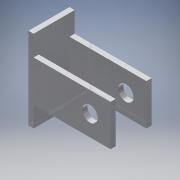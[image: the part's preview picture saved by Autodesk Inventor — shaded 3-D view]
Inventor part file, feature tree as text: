
AUTODESK INVENTOR PART (.ipt)
format: ipt  version: 2016 (Build 200138000, 138)  size: 128,000 bytes
history: native  units: in
note: dims shown in document units (in); Inventor stores cm internally (conversion verified against a paired STEP export)
features: extrude x4, sketch x4
ambient origin geometry x8: Origin, YZ Plane, XZ Plane, XY Plane, X Axis, Y Axis, Z Axis, Center Point
bodies: Solid1 (feature_tree)
feature tree (8):
  extrude  "Extrusion1"  Depth=0.125in
  extrude  "Extrusion2"  Depth=2.0in
  extrude  "Extrusion3"  Depth=0.5in TaperAngle=0.0deg
  extrude  "Extrusion4"  Depth=1.0in
  sketch  "Sketch1"  dims[d0=0.125in d1=0.125in]
  sketch  "Sketch2"  dims[d2=0.75in d3=2.0in]
  sketch  "Sketch3"  dims[d4=1.0in d5=0.0in d6=0.5in d7=0.0in]
  sketch  "Sketch4"  dims[d8=0.5in d9=0.0in d10=0.375in d11=0.5in d12=0.5in d13=1.0in d14=0.0in]
